# Revit family: Shade-Draper_Inc.-Skylight
name_source: partatom
category: Specialty Equipment
revit_build: Autodesk Revit 2017 (Build: 20160225_1515(x64)
units: mm (PartAtom-declared; Revit-internal decimal feet)

## family parameters
Cut with Voids When Loaded = No
Host = Face
Part Type = Normal
Room Calculation Point = No
Round Connector Dimension = Use Diameter
Shared = No

## types (1)
- Skylight Flexshade 2
    Apparent Load = 0 VA
    Default Elevation = 4' - 0"
    Description = Motorized solar control
    Fabric Material = Fabric - Draper - Green Screen Revive 5%
    Frame Material = Paint - Draper - White
    Frequency = 60 Hz
    Headbox Depth = 5 13/16"
    Headbox Height = 5 13/16"
    Length = 8' - 0"
    Manufacturer = Draper Inc.
    Model = Skylight Flexshade 2
    Number of Poles = 1
    Phase = 1
    Power Factor = 1
    Product Documentation Link = https://www.draperinc.com
    Product Name = Skylight FlexShade® 2
    Product Page URL = https://www.draperinc.com
    URL = https://www.draperinc.com
    Voltage = 120 V
    Width = 8' - 0"

## geometry (parser evidence)
native form markers: Blend x4, Sweep x7
no freeform markers — native parametric forms only
